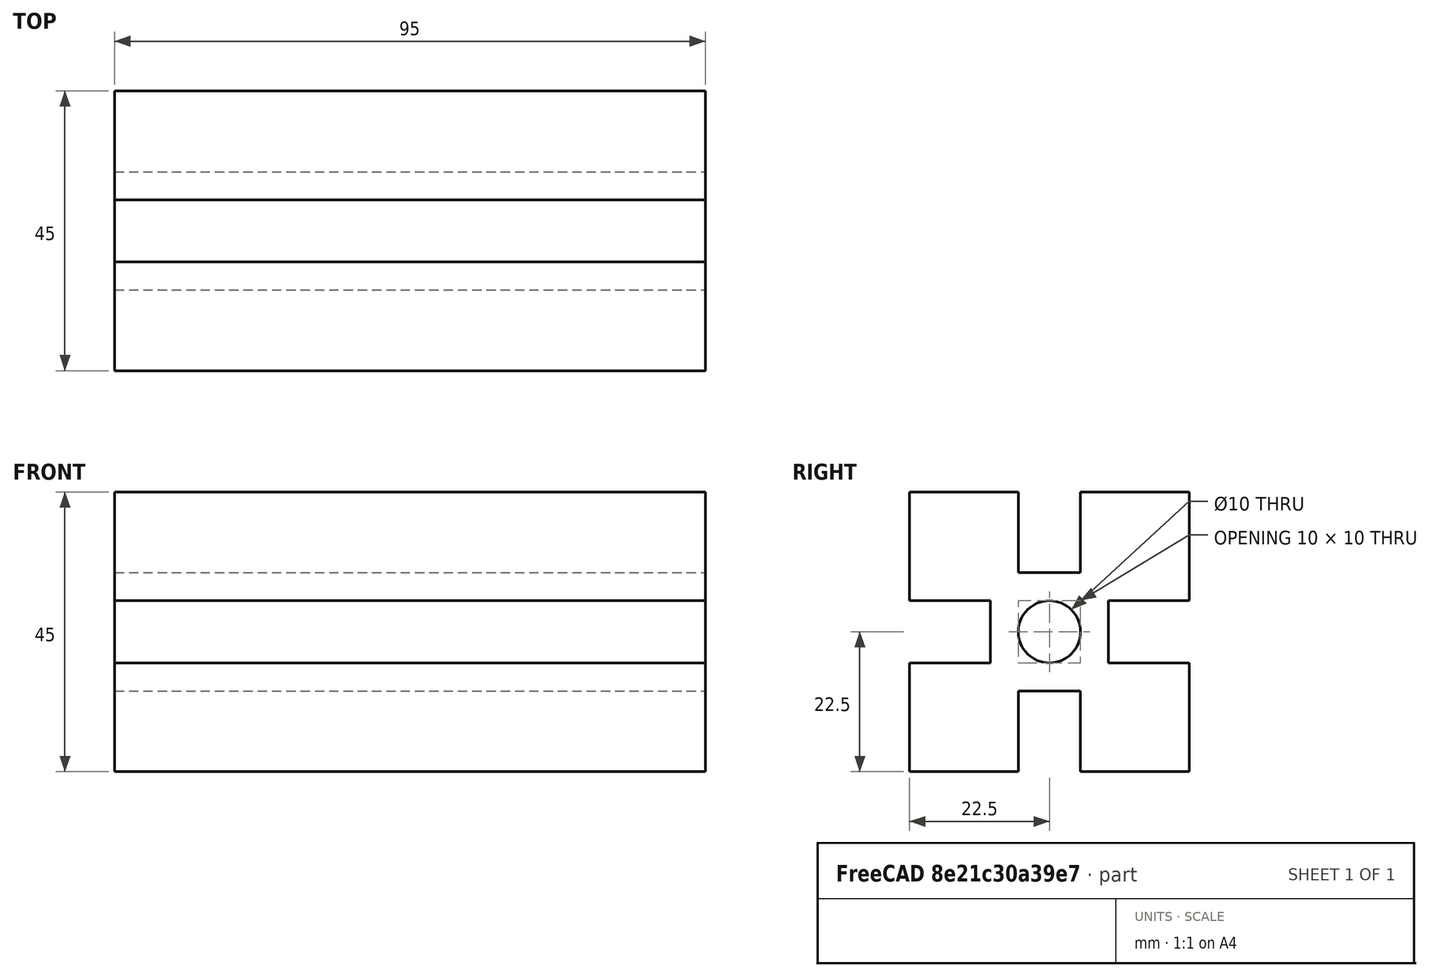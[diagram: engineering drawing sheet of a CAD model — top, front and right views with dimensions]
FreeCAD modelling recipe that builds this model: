
FCSTD DOCUMENT  (FreeCAD 1.0R39109 (Git))
Label: vslot 45x45x95
License: All rights reserved
LicenseURL: https://en.wikipedia.org/wiki/All_rights_reserved
objects: PartDesign::Pocket×4, Part::Feature×1, PartDesign::FeatureBase×1, PartDesign::Pad×1, PartDesign::Body×1
note: 19 computed .brp shape members not serialized (recipe doc carries the construction recipe); baked Part::Feature solids carry a one-line shape summary decoded from their .brp

FEATURE [Part::Feature] Part__Feature  label="1"
  shape: bbox 1000 x 45 x 45 mm, 24 faces (baked)
FEATURE [PartDesign::FeatureBase] BaseFeature
  BaseFeature = -> Part__Feature
  Suppressed = false
FEATURE [PartDesign::Pad] Pad
  BaseFeature = -> BaseFeature
  Direction = (1,0,0)
  Length = 220
  Length2 = 10
  Profile = -> BaseFeature [Face24]
  Refine = true
  Suppressed = false
  Type = 0
FEATURE [PartDesign::Pocket] Pocket
  BaseFeature = -> Pad
  Direction = (-1,0,0)
  Length = 140
  Length2 = 5
  Profile = -> Pad [Face3]
  Refine = true
  Suppressed = false
  Type = 0
FEATURE [PartDesign::Pocket] Pocket001
  BaseFeature = -> Pocket
  Direction = (-1,0,0)
  Length = 480
  Length2 = 5
  Profile = -> Pocket [Face23]
  Refine = true
  Suppressed = false
  Type = 0
FEATURE [PartDesign::Pocket] Pocket002
  BaseFeature = -> Pocket001
  Direction = (-1,0,0)
  Length = 195
  Length2 = 5
  Profile = -> Pocket001 [Face23]
  Refine = true
  Suppressed = false
  Type = 0
FEATURE [PartDesign::Pocket] Pocket003
  BaseFeature = -> Pocket002
  Direction = (-1,0,0)
  Length = 310
  Length2 = 5
  Profile = -> Pocket002 [Face23]
  Refine = true
  Suppressed = false
  Type = 0
FEATURE [PartDesign::Body] Body
  AllowCompound = false
  BaseFeature = -> Part__Feature
  Group = -> [BaseFeature,Pad,Pocket,Pocket001,Pocket002,Pocket003]
  Origin = -> Origin
  Tip = -> Pocket003
